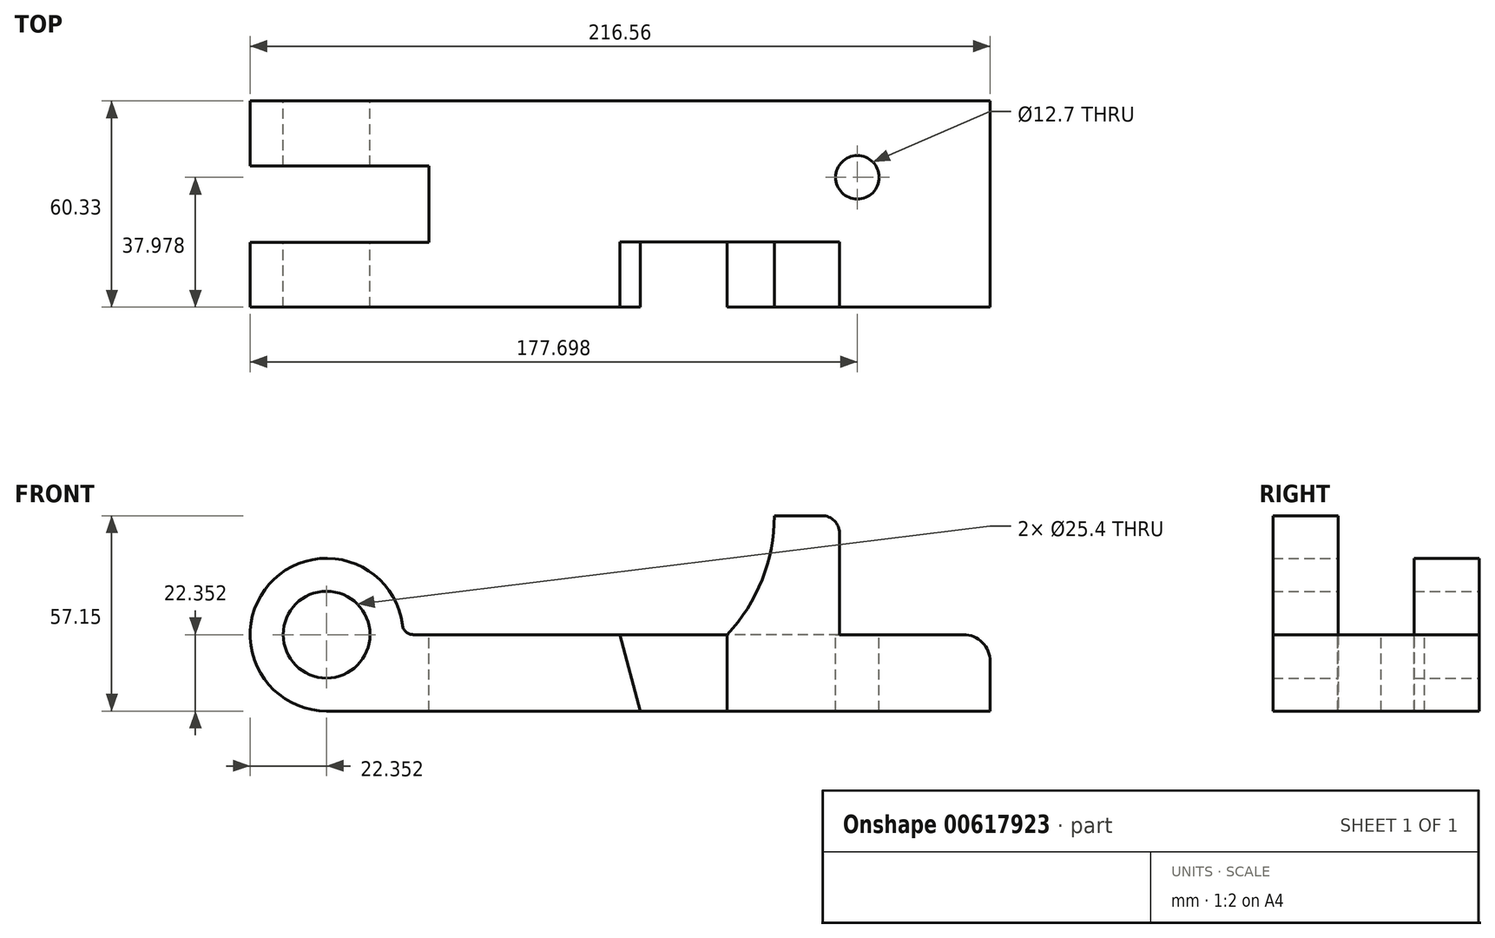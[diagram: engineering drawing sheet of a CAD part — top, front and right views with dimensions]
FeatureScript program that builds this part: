
annotation { "Feature Type Name" : "Feature", "Feature Type Description" : "" }
export const myFeature = defineFeature(function(context is Context, id is Id, definition is map)
    precondition{}
    {
        {
            var Q0;
            Q0=qCreatedBy(makeId("Front.planeOp"),FACE);
            var sketch = newSketch(context, id + "F0", { "sketchPlane" : qUnion([Q0])});
            skLineSegment(sketch, "E0", {"start": v(0, 0) * mm, "end": v(0, 14.48) * mm});
            skLineSegment(sketch, "E1", {"start": v(-7.87, 22.35) * mm, "end": v(-44.12, 22.35) * mm});
            skLineSegment(sketch, "E2", {"start": v(-44.12, 22.35) * mm, "end": v(-44.12, 52.07) * mm});
            skLineSegment(sketch, "E3", {"start": v(-49.2, 57.15) * mm, "end": v(-76.96, 57.15) * mm});
            skLineSegment(sketch, "E4", {"start": v(-76.96, 57.15) * mm, "end": v(-76.96, 22.35) * mm});
            skLineSegment(sketch, "E5", {"start": v(-76.96, 22.35) * mm, "end": v(-171.86, 22.35) * mm});
            skLineSegment(sketch, "E6", {"start": v(-194.2, 0) * mm, "end": v(0, 0) * mm});
            skArc(sketch, "E7", {"start": v(-171.86, 22.35) * mm, "mid": v(-210.01, 38.16) * mm, "end": v(-194.2, 0) * mm});
            skCircle(sketch, "E8", {"center": v(-194.2, 22.35) * mm, "radius": 12.7 * mm});
            skCircle(sketch, "E9", {"center": v(-113.97, 57.15) * mm, "radius": 50.8 * mm});
            skLineSegment(sketch, "E10", {"start": v(-76.96, 22.35) * mm, "end": v(-76.96, 0) * mm});
            skLineSegment(sketch, "E11", {"start": v(-108.36, 22.35) * mm, "end": v(-102.36, 0) * mm});
            skPoint(sketch, "E12.visualSharp", {"position": v(-44.12, 57.15) * mm});
            skArc(sketch, "E12.filletArc", {"start": v(-44.12, 52.07) * mm, "mid": v(-45.6, 55.66) * mm, "end": v(-49.2, 57.15) * mm});
            skPoint(sketch, "E13.visualSharp", {"position": v(0, 22.35) * mm});
            skArc(sketch, "E13.filletArc", {"start": v(0, 14.48) * mm, "mid": v(-2.3, 20.05) * mm, "end": v(-7.87, 22.35) * mm});
            skLineSegment(sketch, "E14", {"start": v(-44.12, 22.35) * mm, "end": v(-76.96, 22.35) * mm});
            skLineSegment(sketch, "E15", {"start": v(-194.2, 22.35) * mm, "end": v(-194.2, 9.65) * mm, "construction": true});
            skLineSegment(sketch, "E16.trimOffspring", {"start": v(-194.2, 59.62) * mm, "end": v(-194.2, 0) * mm, "construction": true});
            skSolve(sketch);
        }
        {
            var Q0;
            {var subQ0=sQuery(id+"F0.wireOp",EDGE,"E7");Q0=makeQuery(id+"F0.imprint","IMPRINT",FACE,{"disambiguationData":[TD([[makeQuery(id+"F0.imprint","IMPRINT",EDGE,{"derivedFrom":subQ0}),1.0]])]});}
            var Q1;
            {var subQ0=sQuery(id+"F0.wireOp",EDGE,"E11");var subQ1=sQuery(id+"F0.wireOp",EDGE,"E5");var subQ2=makeQuery(id+"F0.imprint","INTERSECT",VERTEX,{"derivedFrom":[subQ1,subQ0]});Q1=makeQuery(id+"F0.imprint","IMPRINT",FACE,{"disambiguationData":[TD([[makeQuery(id+"F0.imprint","IMPRINT",EDGE,{"disambiguationData":[TD([[subQ2,-1.0]])],"derivedFrom":subQ1}),1.0]])]});}
            var Q2;
            {var subQ1=sQuery(id+"F0.wireOp",EDGE,"E5");var subQ3=sQuery(id+"F0.wireOp",EDGE,"E11");var subQ4=makeQuery(id+"F0.imprint","INTERSECT",VERTEX,{"derivedFrom":[subQ1,subQ3]});Q2=makeQuery(id+"F0.imprint","IMPRINT",FACE,{"disambiguationData":[TD([[makeQuery(id+"F0.imprint","IMPRINT",EDGE,{"disambiguationData":[TD([[subQ4,-1.0]])],"derivedFrom":subQ3}),1.0]])]});}
            var Q3;
            {var subQ0=sQuery(id+"F0.wireOp",EDGE,"E10");Q3=makeQuery(id+"F0.imprint","IMPRINT",FACE,{"disambiguationData":[TD([[makeQuery(id+"F0.imprint","IMPRINT",EDGE,{"derivedFrom":subQ0}),-1.0]])]});}
            var Q4;
            {var subQ2=sQuery(id+"F0.wireOp",EDGE,"E0");Q4=makeQuery(id+"F0.imprint","IMPRINT",FACE,{"disambiguationData":[TD([[makeQuery(id+"F0.imprint","IMPRINT",EDGE,{"derivedFrom":subQ2}),1.0]])]});}
            extrude(context, id + "F1", {"entities" : qUnion([Q0, Q1, Q2, Q3, Q4]), "depth" : 60.32 * mm});
        }
        {
            var Q0;
            Q0=makeQuery(id+"F1.opExtrude","CAP_FACE",FACE,{"disambiguationData":[OSD([sQuery(id+"F0.wireOp",EDGE,"E0"),sQuery(id+"F0.wireOp",EDGE,"E1"),sQuery(id+"F0.wireOp",EDGE,"E5"),sQuery(id+"F0.wireOp",EDGE,"E6"),sQuery(id+"F0.wireOp",EDGE,"E7"),sQuery(id+"F0.wireOp",EDGE,"E8"),sQuery(id+"F0.wireOp",EDGE,"E13.filletArc"),sQuery(id+"F0.wireOp",EDGE,"E14")])],"isStart":false});
            var sketch = newSketch(context, id + "F2", { "sketchPlane" : qUnion([Q0])});
            skLineSegment(sketch, "E17.0", {"start": v(-76.96, 22.35) * mm, "end": v(-76.96, 0) * mm});
            skLineSegment(sketch, "E18.0", {"start": v(-108.36, 22.35) * mm, "end": v(-102.36, 0) * mm});
            skLineSegment(sketch, "E19.0", {"start": v(-49.2, 57.15) * mm, "end": v(-76.96, 57.15) * mm});
            skCircle(sketch, "E20.0", {"center": v(-113.97, 57.15) * mm, "radius": 50.8 * mm});
            skLineSegment(sketch, "E21.0", {"start": v(-76.96, 57.15) * mm, "end": v(-76.96, 22.35) * mm});
            skLineSegment(sketch, "E22.0", {"start": v(-76.96, 22.35) * mm, "end": v(-171.86, 22.35) * mm});
            skLineSegment(sketch, "E23.0", {"start": v(-194.2, 0) * mm, "end": v(0, 0) * mm});
            skLineSegment(sketch, "E24.0", {"start": v(-44.12, 22.35) * mm, "end": v(-44.12, 52.07) * mm});
            skArc(sketch, "E25.0", {"start": v(-44.12, 52.07) * mm, "mid": v(-45.6, 55.66) * mm, "end": v(-49.2, 57.15) * mm});
            skLineSegment(sketch, "E26.0", {"start": v(-44.12, 22.35) * mm, "end": v(-76.96, 22.35) * mm});
            skSolve(sketch);
        }
        {
            var Q0;
            Q0=makeQuery(id+"F2.imprint","IMPRINT",FACE,{"disambiguationData":[TD([[makeQuery(id+"F2.imprint","IMPRINT",EDGE,{"derivedFrom":sQuery(id+"F2.wireOp",EDGE,"E24.0")}),1.0]])]});
            extrude(context, id + "F3", {"entities" : qUnion([Q0]), "operationType" : NewBodyOperationType.ADD, "oppositeDirection" : true, "depth" : 19.05 * mm});
        }
        {
            var Q0;
            {var subQ0=sQuery(id+"F2.wireOp",EDGE,"E22.0");var subQ1=sQuery(id+"F2.wireOp",EDGE,"E18.0");var subQ2=makeQuery(id+"F2.imprint","INTERSECT",VERTEX,{"derivedFrom":[subQ1,subQ0]});Q0=makeQuery(id+"F2.imprint","IMPRINT",FACE,{"disambiguationData":[TD([[makeQuery(id+"F2.imprint","IMPRINT",EDGE,{"disambiguationData":[TD([[subQ2,-1.0]])],"derivedFrom":subQ1}),1.0]])]});}
            var Q1;
            {var subQ0=sQuery(id+"F2.wireOp",EDGE,"E17.0");Q1=makeQuery(id+"F2.imprint","IMPRINT",FACE,{"disambiguationData":[TD([[makeQuery(id+"F2.imprint","IMPRINT",EDGE,{"derivedFrom":subQ0}),-1.0]])]});}
            extrude(context, id + "F4", {"entities" : qUnion([Q0, Q1]), "operationType" : NewBodyOperationType.REMOVE, "oppositeDirection" : true, "depth" : 19.05 * mm});
        }
        {
            var Q0;
            Q0=makeQuery(id+"F1.opExtrude","SWEPT_FACE",FACE,{"disambiguationData":[OSD([sQuery(id+"F0.wireOp",EDGE,"E1"),sQuery(id+"F0.wireOp",EDGE,"E5"),sQuery(id+"F0.wireOp",EDGE,"E14")])]});
            var sketch = newSketch(context, id + "F5", { "sketchPlane" : qUnion([Q0])});
            skCircle(sketch, "E27", {"center": v(-38.86, -22.35) * mm, "radius": 6.35 * mm});
            skSolve(sketch);
        }
        {
            var Q0;
            Q0=qSketchRegion(id+"F5",true);
            var Q1;
            Q1=makeQuery(id+"F1.opExtrude","SWEPT_FACE",FACE,{"disambiguationData":[OSD([sQuery(id+"F0.wireOp",EDGE,"E6")])]});
            extrude(context, id + "F6", {"entities" : qUnion([Q0]), "operationType" : NewBodyOperationType.REMOVE, "endBound" : BoundingType.UP_TO_SURFACE, "oppositeDirection" : true, "endBoundEntityFace" : qUnion([Q1]), "depth" : 25.4 * mm});
        }
        {
            var Q0;
            Q0=makeQuery(id+"F1.opExtrude","SWEPT_FACE",FACE,{"disambiguationData":[OSD([sQuery(id+"F0.wireOp",EDGE,"E1"),sQuery(id+"F0.wireOp",EDGE,"E5"),sQuery(id+"F0.wireOp",EDGE,"E14")])]});
            var sketch = newSketch(context, id + "F7", { "sketchPlane" : qUnion([Q0])});
            skLineSegment(sketch, "E28.bottom", {"start": v(-233.73, -19) * mm, "end": v(-164.24, -19) * mm});
            skLineSegment(sketch, "E28.top", {"start": v(-233.73, -41.33) * mm, "end": v(-164.24, -41.33) * mm});
            skLineSegment(sketch, "E28.left", {"start": v(-233.73, -19) * mm, "end": v(-233.73, -41.33) * mm});
            skLineSegment(sketch, "E28.right", {"start": v(-164.24, -19) * mm, "end": v(-164.24, -41.33) * mm});
            skSolve(sketch);
        }
        {
            var Q0;
            Q0=makeQuery(id+"F1.opExtrude","SWEPT_EDGE",EDGE,{"disambiguationData":[OSD([sQuery(id+"F0.wireOp",EDGE,"E5"),sQuery(id+"F0.wireOp",EDGE,"E7")])]});
            var Q1;
            Q1=makeQuery(id+"F3.opExtrude","SWEPT_EDGE",EDGE,{"disambiguationData":[OSD([sQuery(id+"F0.wireOp",EDGE,"E1"),sQuery(id+"F0.wireOp",EDGE,"E5"),sQuery(id+"F0.wireOp",EDGE,"E14"),sQuery(id+"F2.wireOp",EDGE,"E24.0"),sQuery(id+"F2.wireOp",EDGE,"E26.0")])]});
            fillet(context, id + "F8", {"entities" : qUnion([Q0, Q1]), "radius" : 3.3 * mm, "tangentPropagation" : true, "allowEdgeOverflow" : false});
        }
        {
            var Q0;
            Q0=qSketchRegion(id+"F7",true);
            extrude(context, id + "F9", {"entities" : qUnion([Q0]), "operationType" : NewBodyOperationType.REMOVE, "endBound" : BoundingType.SYMMETRIC, "oppositeDirection" : true, "depth" : 127 * mm});
        }
    });
